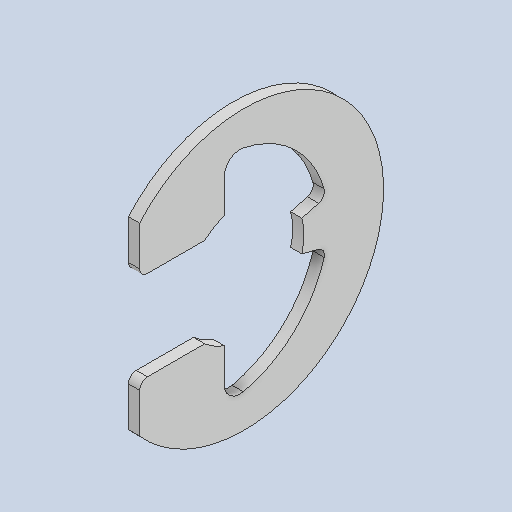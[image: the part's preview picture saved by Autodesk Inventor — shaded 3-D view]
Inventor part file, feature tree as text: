
AUTODESK INVENTOR PART (.ipt)
format: ipt  version: 2023 (Build 270158030, 158C)  size: 109,568 bytes
history: native  units: in
note: dims shown in document units (in); Inventor stores cm internally (conversion verified against a paired STEP export)
features: fillet x1
ambient origin geometry x8: Origin, YZ Plane, XZ Plane, XY Plane, X Axis, Y Axis, Z Axis, Center Point
bodies: Solid1 (feature_tree)
feature tree (1):
  fillet  "Fillet2"  [1 undecoded]
note: 1 required parameter value undecoded (feature->parameter linkage not recoverable at this tier; creation-order binding heuristic only, values carry confidence <= 0.55)
